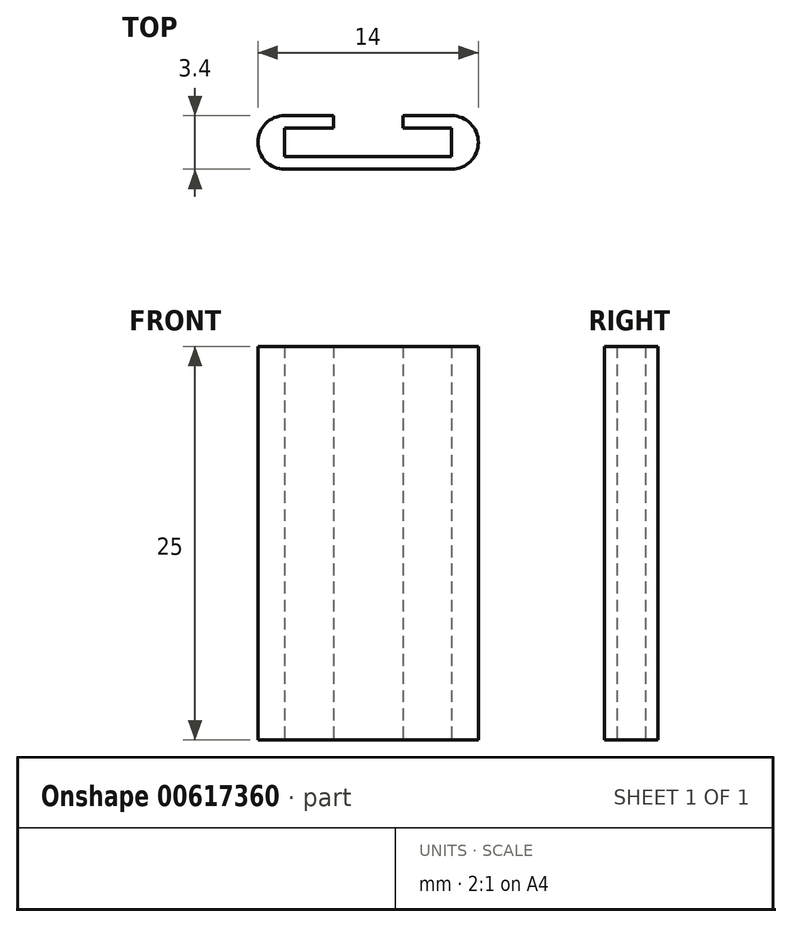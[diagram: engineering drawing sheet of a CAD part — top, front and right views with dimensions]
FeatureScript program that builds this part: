
annotation { "Feature Type Name" : "Feature", "Feature Type Description" : "" }
export const myFeature = defineFeature(function(context is Context, id is Id, definition is map)
    precondition{}
    {
        {
            var Q0;
            Q0=qCreatedBy(makeId("Top.planeOp"),FACE);
            var sketch = newSketch(context, id + "F0", { "sketchPlane" : qUnion([Q0])});
            skLineSegment(sketch, "E0", {"start": v(0, 0) * mm, "end": v(5.3, 0) * mm});
            skLineSegment(sketch, "E1", {"start": v(5.3, 0) * mm, "end": v(5.3, 1.8) * mm});
            skLineSegment(sketch, "E2", {"start": v(5.3, 1.8) * mm, "end": v(2.2, 1.8) * mm});
            skLineSegment(sketch, "E3", {"start": v(2.2, 1.8) * mm, "end": v(2.2, 2.6) * mm});
            skLineSegment(sketch, "E4", {"start": v(2.2, 2.6) * mm, "end": v(5.3, 2.6) * mm});
            skArc(sketch, "E5", {"start": v(5.3, -0.8) * mm, "mid": v(7, 0.9) * mm, "end": v(5.3, 2.6) * mm});
            skLineSegment(sketch, "E6", {"start": v(0, 0) * mm, "end": v(0, -0.8) * mm, "construction": true});
            skLineSegment(sketch, "E7", {"start": v(0, -0.8) * mm, "end": v(5.3, -0.8) * mm});
            skLineSegment(sketch, "E8.MirrorCS", {"start": v(0, 0) * mm, "end": v(-5.3, 0) * mm});
            skLineSegment(sketch, "E9.MirrorCS", {"start": v(-5.3, 0) * mm, "end": v(-5.3, 1.8) * mm});
            skLineSegment(sketch, "E10.MirrorCS", {"start": v(-5.3, 1.8) * mm, "end": v(-2.2, 1.8) * mm});
            skLineSegment(sketch, "E11.MirrorCS", {"start": v(-2.2, 1.8) * mm, "end": v(-2.2, 2.6) * mm});
            skLineSegment(sketch, "E12.MirrorCS", {"start": v(-2.2, 2.6) * mm, "end": v(-5.3, 2.6) * mm});
            skArc(sketch, "E13.MirrorCS", {"start": v(-5.3, -0.8) * mm, "mid": v(-7, 0.9) * mm, "end": v(-5.3, 2.6) * mm});
            skLineSegment(sketch, "E14.MirrorCS", {"start": v(0, -0.8) * mm, "end": v(-5.3, -0.8) * mm});
            skSolve(sketch);
        }
        {
            var Q0;
            Q0=makeQuery(id+"F0.imprint","IMPRINT",FACE,{"disambiguationData":[TD([[makeQuery(id+"F0.imprint","IMPRINT",EDGE,{"derivedFrom":sQuery(id+"F0.wireOp",EDGE,"E0")}),-1.0]])]});
            extrude(context, id + "F1", {"entities" : qUnion([Q0]), "depth" : 25 * mm, "offsetDistance" : 25 * mm});
        }
    });
